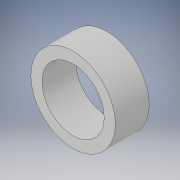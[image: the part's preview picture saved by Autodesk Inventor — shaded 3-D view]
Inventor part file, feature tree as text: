
AUTODESK INVENTOR PART (.ipt)
format: ipt  version: 2019 (Build 230136000, 136)  size: 102,912 bytes
history: native  units: mm
features: extrude x2, sketch x2
ambient origin geometry x8: Origin, YZ Plane, XZ Plane, XY Plane, X Axis, Y Axis, Z Axis, Center Point
bodies: Solid1 (feature_tree)
feature tree (4):
  extrude  "Extrusion1"  Depth=202.45mm TaperAngle=0.0deg
  extrude  "Extrusion2"  Depth=20.245mm TaperAngle=0.0deg
  sketch  "Sketch1"  dims[d0=504.2mm d1=202.45mm d2=0.0mm]
  sketch  "Sketch2"  dims[d3=371.4mm d4=20.245mm d5=0.0mm]
